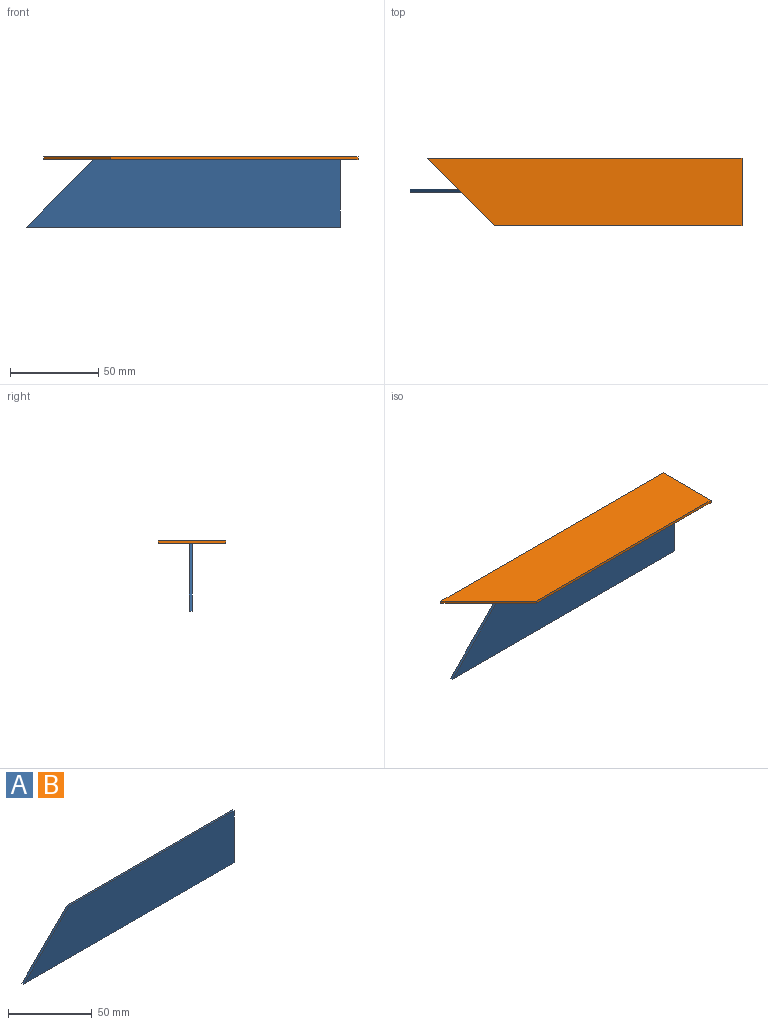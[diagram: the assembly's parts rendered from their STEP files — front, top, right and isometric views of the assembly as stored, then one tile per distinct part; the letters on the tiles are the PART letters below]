
ASSEMBLY  parts=2 mates=1
PART A: 6 faces, bbox 177.8x1.6x38.1 mm
  f0: plane 139.7x1.59mm, normal (0,0,1), area 221.8mm2, adj f1,f3,f4,f5
  f1: plane 38.1x38.1mm, normal (-0.71,0,0.71), area 85.5mm2, adj f0,f2,f4,f5
  f2: plane 177.8x1.59mm, normal (0,0,-1), area 282.3mm2, adj f1,f3,f4,f5
  f3: plane 38.1x1.59mm, normal (1,0,0), area 60.5mm2, adj f0,f2,f4,f5
  f4: plane 177.8x38.1mm, normal (0,-1,0), area 6048.4mm2, adj f0,f1,f2,f3
  f5: plane 177.8x38.1mm, normal (0,1,0), area 6048.4mm2, adj f0,f1,f2,f3
PART B: same geometry as A
PLACE A t=(18.43,-21.72,23.17)mm
PLACE B rot(axis=(1,0,0),90deg) t=(28.33,-3.44,62.06)mm
MATE fastened B.f4 <-> A.f0  axis (0,0,-1) through (37.48,-21.72,61.27)mm
